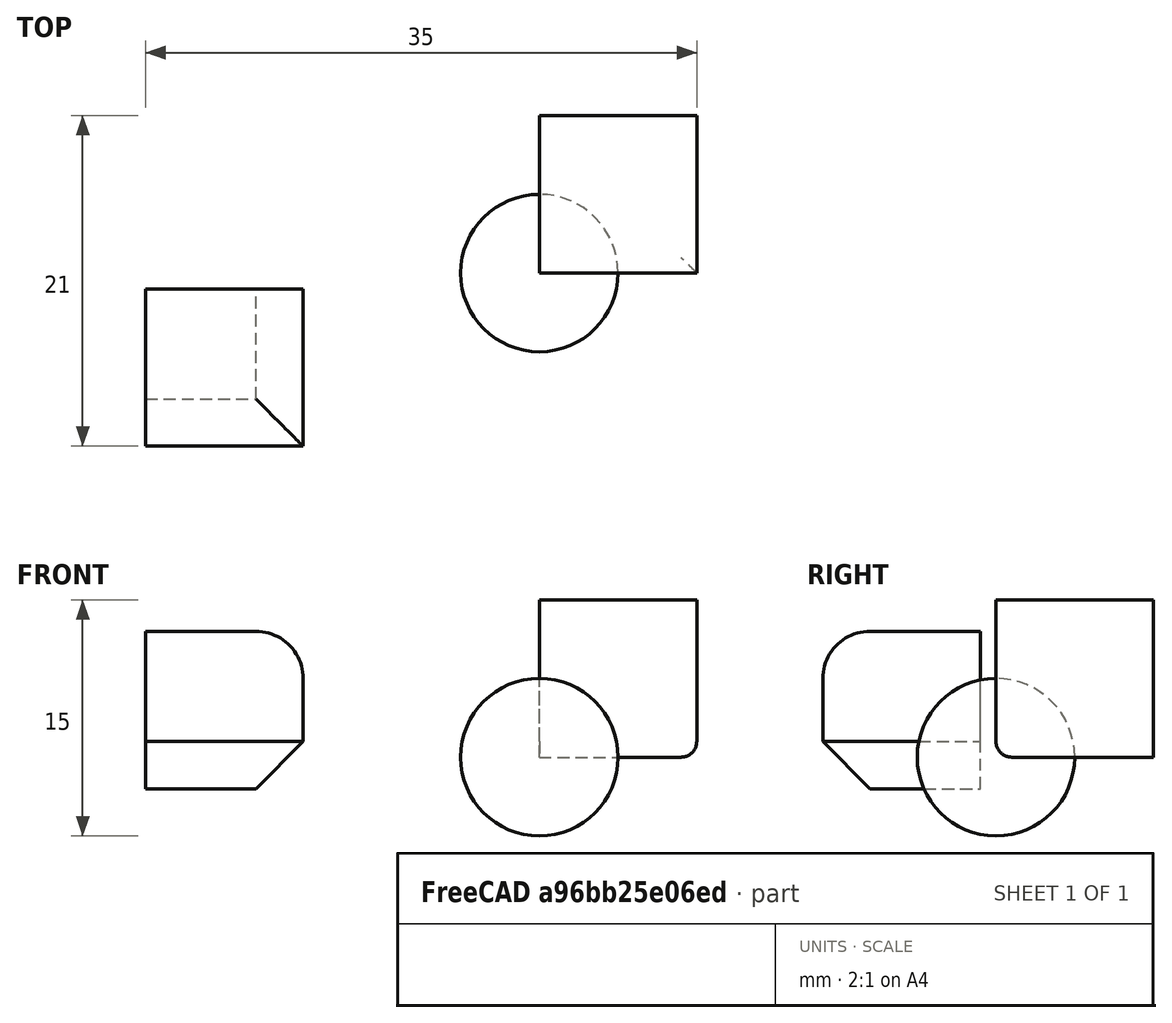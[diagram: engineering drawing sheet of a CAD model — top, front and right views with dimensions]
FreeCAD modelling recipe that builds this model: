
FCSTD DOCUMENT  (FreeCAD 0.18R16117 (Git))
Label: First experiment tutorials
License: All rights reserved
LicenseURL: http://en.wikipedia.org/wiki/All_rights_reserved
objects: Part::Box×2, Part::Fillet×2, Part::Sphere×1, Part::Chamfer×1
note: 6 computed .brp shape members not serialized (recipe doc carries the construction recipe); baked Part::Feature solids carry a one-line shape summary decoded from their .brp

FEATURE [Part::Box] Box  label="Cube"
  AttacherType = Attacher::AttachEngine3D
  Height = 10
  Length = 10
  Placement = pos=(7,7,-2) rot=(0,0,1;0rad)
  Width = 10
FEATURE [Part::Sphere] Sphere
  Angle1 = -90
  Angle2 = 90
  Angle3 = 360
  AttacherType = Attacher::AttachEngine3D
  Placement = pos=(7,7,-2) rot=(0,0,1;0rad)
  Radius = 5
FEATURE [Part::Box] Box001  label="another cube"
  AttacherType = Attacher::AttachEngine3D
  Height = 10
  Length = 10
  Placement = pos=(-18,-4,-4) rot=(0,0,1;0rad)
  Width = 10
FEATURE [Part::Fillet] Fillet
  Base = -> Box001
  Edges = 2 edges r=3: [Edge6,Edge10]
FEATURE [Part::Chamfer] Chamfer
  Base = -> Fillet
  Edges = 2 edges r=3: [Edge8,Edge12]
FEATURE [Part::Fillet] Fillet001
  Base = -> Box
  Edges = 2 edges r=1: [Edge8,Edge9]
